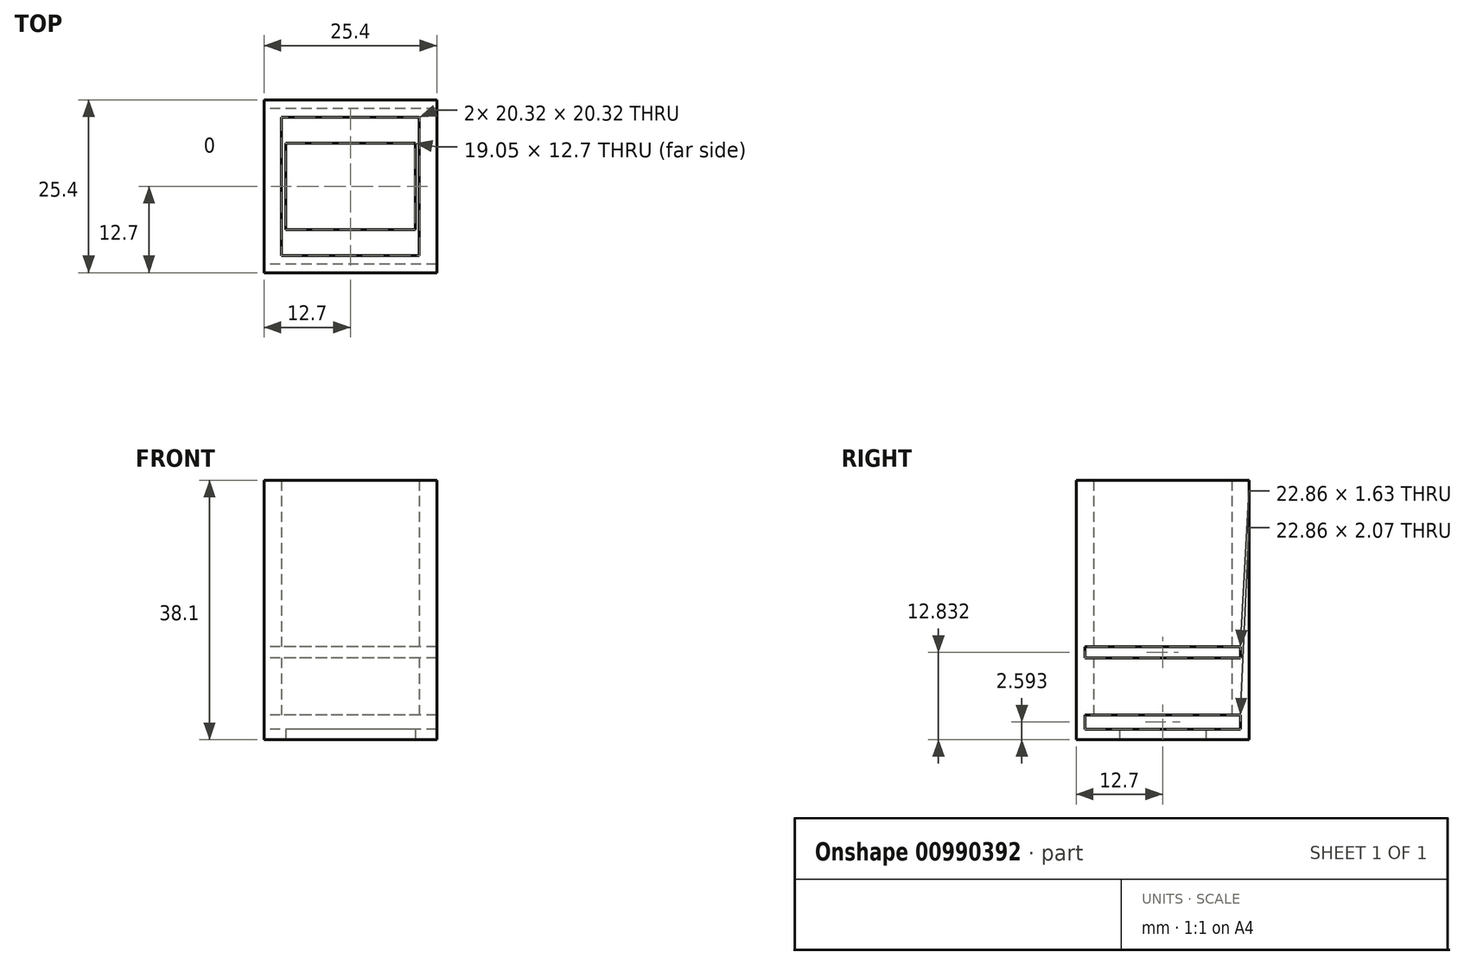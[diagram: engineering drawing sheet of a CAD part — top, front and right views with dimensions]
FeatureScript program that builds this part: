
annotation { "Feature Type Name" : "Feature", "Feature Type Description" : "" }
export const myFeature = defineFeature(function(context is Context, id is Id, definition is map)
    precondition{}
    {
        {
            var Q0;
            Q0=qCreatedBy(makeId("Top.planeOp"),FACE);
            var sketch = newSketch(context, id + "F0", { "sketchPlane" : qUnion([Q0])});
            skLineSegment(sketch, "E0.bottom", {"start": v(-12.7, -12.7) * mm, "end": v(12.7, -12.7) * mm});
            skLineSegment(sketch, "E0.top", {"start": v(-12.7, 12.7) * mm, "end": v(12.7, 12.7) * mm});
            skLineSegment(sketch, "E0.left", {"start": v(-12.7, -12.7) * mm, "end": v(-12.7, 12.7) * mm});
            skLineSegment(sketch, "E0.right", {"start": v(12.7, -12.7) * mm, "end": v(12.7, 12.7) * mm});
            skPoint(sketch, "E0.middle", {"position": v(0, 0) * mm});
            skSolve(sketch);
        }
        {
            var Q0;
            Q0=makeQuery(id+"F0.imprint","IMPRINT",FACE,{"disambiguationData":[TD([[makeQuery(id+"F0.imprint","IMPRINT",EDGE,{"derivedFrom":sQuery(id+"F0.wireOp",EDGE,"E0.bottom")}),1.0]])]});
            extrude(context, id + "F1", {"entities" : qUnion([Q0]), "depth" : 38.1 * mm, "offsetDistance" : 25.4 * mm});
        }
        {
            var Q0;
            Q0=makeQuery(id+"F1.opExtrude","CAP_FACE",FACE,{"disambiguationData":[OSD([sQuery(id+"F0.wireOp",EDGE,"E0.bottom"),sQuery(id+"F0.wireOp",EDGE,"E0.top"),sQuery(id+"F0.wireOp",EDGE,"E0.left"),sQuery(id+"F0.wireOp",EDGE,"E0.right")])],"isStart":false});
            shell(context, id + "F2", {"entities" : qUnion([Q0]), "thickness" : 2.54 * mm});
        }
        {
            var Q0;
            Q0=qCreatedBy(makeId("Top.planeOp"),FACE);
            var sketch = newSketch(context, id + "F3", { "sketchPlane" : qUnion([Q0])});
            skLineSegment(sketch, "E1.bottom", {"start": v(-9.52, 6.35) * mm, "end": v(9.53, 6.35) * mm});
            skLineSegment(sketch, "E1.top", {"start": v(-9.53, -6.35) * mm, "end": v(9.52, -6.35) * mm});
            skLineSegment(sketch, "E1.left", {"start": v(-9.52, 6.35) * mm, "end": v(-9.53, -6.35) * mm});
            skLineSegment(sketch, "E1.right", {"start": v(9.53, 6.35) * mm, "end": v(9.52, -6.35) * mm});
            skPoint(sketch, "E1.middle", {"position": v(0, 0) * mm});
            skSolve(sketch);
        }
        {
            var Q0;
            Q0 = qSketchRegion(id + "F3", true);
            var Q1;
            Q1=makeQuery(id+"F3.imprint","IMPRINT",FACE,{"disambiguationData":[TD([[makeQuery(id+"F3.imprint","IMPRINT",EDGE,{"derivedFrom":sQuery(id+"F3.wireOp",EDGE,"E1.bottom")}),-1.0]])]});
            extrude(context, id + "F4", {"entities" : qUnion([Q0, Q1]), "operationType" : NewBodyOperationType.REMOVE, "depth" : 25.4 * mm, "offsetDistance" : 25.4 * mm});
        }
        {
            var Q0;
            Q0=qCreatedBy(makeId("Right.planeOp"),FACE);
            var sketch = newSketch(context, id + "F5", { "sketchPlane" : qUnion([Q0])});
            skLineSegment(sketch, "E2.bottom", {"start": v(11.43, 1.56) * mm, "end": v(-11.43, 1.56) * mm});
            skLineSegment(sketch, "E2.top", {"start": v(11.43, 3.63) * mm, "end": v(-11.43, 3.63) * mm});
            skLineSegment(sketch, "E2.left", {"start": v(11.43, 1.56) * mm, "end": v(11.43, 3.63) * mm});
            skLineSegment(sketch, "E2.right", {"start": v(-11.43, 1.56) * mm, "end": v(-11.43, 3.63) * mm});
            skPoint(sketch, "E2.middle", {"position": v(0, 2.6) * mm});
            skSolve(sketch);
        }
        {
            var Q0;
            Q0=makeQuery(id+"F5.imprint","IMPRINT",FACE,{"disambiguationData":[TD([[makeQuery(id+"F5.imprint","IMPRINT",EDGE,{"derivedFrom":sQuery(id+"F5.wireOp",EDGE,"E2.bottom")}),-1.0]])]});
            var Q1;
            Q1=sQuery(id+"F5.wireOp",EDGE,"E2.top");
            var Q2;
            Q2=sQuery(id+"F5.wireOp",EDGE,"E2.bottom");
            extrude(context, id + "F6", {"entities" : qUnion([Q0]), "operationType" : NewBodyOperationType.REMOVE, "surfaceEntities" : qUnion([Q1, Q2]), "depth" : 25.4 * mm, "offsetDistance" : 25.4 * mm, "hasSecondDirection" : true, "secondDirectionOppositeDirection" : true, "secondDirectionDepth" : 25.4 * mm});
        }
        {
            var Q0;
            Q0=qCreatedBy(makeId("Right.planeOp"),FACE);
            var sketch = newSketch(context, id + "F7", { "sketchPlane" : qUnion([Q0])});
            skLineSegment(sketch, "E3.bottom", {"start": v(11.43, 12.01) * mm, "end": v(-11.43, 12.01) * mm});
            skLineSegment(sketch, "E3.top", {"start": v(11.43, 13.65) * mm, "end": v(-11.43, 13.65) * mm});
            skLineSegment(sketch, "E3.left", {"start": v(11.43, 12.01) * mm, "end": v(11.43, 13.65) * mm});
            skLineSegment(sketch, "E3.right", {"start": v(-11.43, 12.01) * mm, "end": v(-11.43, 13.65) * mm});
            skPoint(sketch, "E3.middle", {"position": v(0, 12.83) * mm});
            skSolve(sketch);
        }
        {
            var Q0;
            Q0=makeQuery(id+"F7.imprint","IMPRINT",FACE,{"disambiguationData":[TD([[makeQuery(id+"F7.imprint","IMPRINT",EDGE,{"derivedFrom":sQuery(id+"F7.wireOp",EDGE,"E3.bottom")}),-1.0]])]});
            extrude(context, id + "F8", {"entities" : qUnion([Q0]), "operationType" : NewBodyOperationType.REMOVE, "depth" : 25.4 * mm, "offsetDistance" : 25.4 * mm, "hasSecondDirection" : true, "secondDirectionOppositeDirection" : true, "secondDirectionDepth" : 25.4 * mm});
        }
    });
